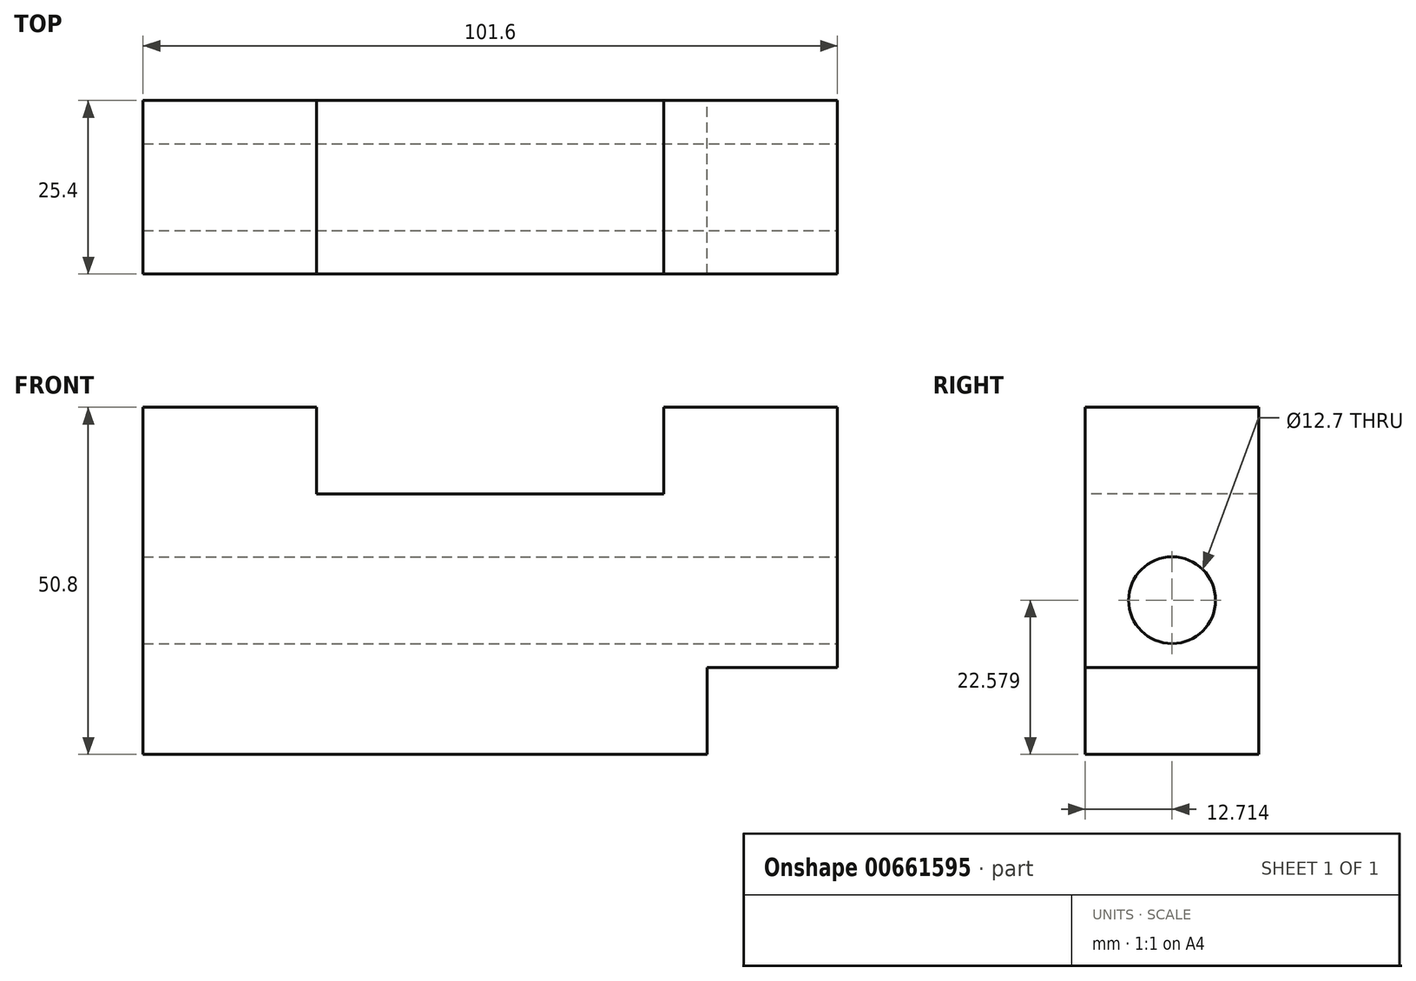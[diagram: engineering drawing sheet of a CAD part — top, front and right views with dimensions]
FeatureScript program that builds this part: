
annotation { "Feature Type Name" : "Feature", "Feature Type Description" : "" }
export const myFeature = defineFeature(function(context is Context, id is Id, definition is map)
    precondition{}
    {
        {
            var Q0;
            Q0=qCreatedBy(makeId("Front.planeOp"),FACE);
            var sketch = newSketch(context, id + "F0", { "sketchPlane" : qUnion([Q0])});
            skLineSegment(sketch, "E0.bottom", {"start": v(0, 0) * mm, "end": v(-101.6, 0) * mm});
            skLineSegment(sketch, "E0.top", {"start": v(0, 50.8) * mm, "end": v(-101.6, 50.8) * mm});
            skLineSegment(sketch, "E0.left", {"start": v(0, 0) * mm, "end": v(0, 50.8) * mm});
            skLineSegment(sketch, "E0.right", {"start": v(-101.6, 0) * mm, "end": v(-101.6, 50.8) * mm});
            skPoint(sketch, "E0.middle", {"position": v(-50.8, 25.4) * mm});
            skSolve(sketch);
        }
        {
            var Q0;
            Q0 = qSketchRegion(id + "F0", true);
            extrude(context, id + "F1", {"entities" : qUnion([Q0]), "depth" : 25.4 * mm, "offsetDistance" : 25.4 * mm});
        }
        {
            var Q0;
            Q0=makeQuery(id+"F1.opExtrude","CAP_FACE",FACE,{"disambiguationData":[OSD([sQuery(id+"F0.wireOp",EDGE,"E0.bottom"),sQuery(id+"F0.wireOp",EDGE,"E0.top"),sQuery(id+"F0.wireOp",EDGE,"E0.left"),sQuery(id+"F0.wireOp",EDGE,"E0.right")])],"isStart":false});
            var sketch = newSketch(context, id + "F2", { "sketchPlane" : qUnion([Q0])});
            skLineSegment(sketch, "E1.bottom", {"start": v(-25.4, 38.1) * mm, "end": v(-76.2, 38.1) * mm});
            skLineSegment(sketch, "E1.top", {"start": v(-25.4, 63.5) * mm, "end": v(-76.2, 63.5) * mm});
            skLineSegment(sketch, "E1.left", {"start": v(-25.4, 38.1) * mm, "end": v(-25.4, 63.5) * mm});
            skLineSegment(sketch, "E1.right", {"start": v(-76.2, 38.1) * mm, "end": v(-76.2, 63.5) * mm});
            skPoint(sketch, "E1.middle", {"position": v(-50.8, 50.8) * mm});
            skSolve(sketch);
        }
        {
            var Q0;
            {var subQ0=sQuery(id+"F2.wireOp",EDGE,"E1.bottom");Q0=makeQuery(id+"F2.imprint","IMPRINT",FACE,{"disambiguationData":[TD([[makeQuery(id+"F2.imprint","IMPRINT",EDGE,{"derivedFrom":subQ0}),-1.0]])]});}
            extrude(context, id + "F3", {"entities" : qUnion([Q0]), "operationType" : NewBodyOperationType.REMOVE, "endBound" : BoundingType.THROUGH_ALL, "oppositeDirection" : true, "depth" : 25.4 * mm, "offsetDistance" : 25.4 * mm});
        }
        {
            var Q0;
            Q0=makeQuery(id+"F1.opExtrude","SWEPT_FACE",FACE,{"disambiguationData":[OSD([sQuery(id+"F0.wireOp",EDGE,"E0.left")])]});
            var sketch = newSketch(context, id + "F4", { "sketchPlane" : qUnion([Q0])});
            skLineSegment(sketch, "E2.bottom", {"start": v(-25.4, 12.7) * mm, "end": v(0, 12.7) * mm});
            skLineSegment(sketch, "E2.top", {"start": v(-25.4, 0) * mm, "end": v(0, 0) * mm});
            skLineSegment(sketch, "E2.left", {"start": v(-25.4, 12.7) * mm, "end": v(-25.4, 0) * mm});
            skLineSegment(sketch, "E2.right", {"start": v(0, 12.7) * mm, "end": v(0, 0) * mm});
            skSolve(sketch);
        }
        {
            var Q0;
            Q0=makeQuery(id+"F4.imprint","IMPRINT",FACE,{"disambiguationData":[TD([[makeQuery(id+"F4.imprint","IMPRINT",EDGE,{"derivedFrom":sQuery(id+"F4.wireOp",EDGE,"E2.bottom")}),-1.0]])]});
            extrude(context, id + "F5", {"entities" : qUnion([Q0]), "operationType" : NewBodyOperationType.REMOVE, "oppositeDirection" : true, "depth" : 19.05 * mm, "offsetDistance" : 25.4 * mm});
        }
        {
            var Q0;
            Q0=makeQuery(id+"F1.opExtrude","SWEPT_FACE",FACE,{"disambiguationData":[OSD([sQuery(id+"F0.wireOp",EDGE,"E0.left")])]});
            var sketch = newSketch(context, id + "F6", { "sketchPlane" : qUnion([Q0])});
            skCircle(sketch, "E3", {"center": v(-12.69, 22.58) * mm, "radius": 6.35 * mm});
            skPoint(sketch, "E3.first.point", {"position": v(-17.65, 18.62) * mm});
            skPoint(sketch, "E3.second.point", {"position": v(-7.93, 26.78) * mm});
            skPoint(sketch, "E3.third.point", {"position": v(-12.18, 28.9) * mm});
            skSolve(sketch);
        }
        {
            var Q0;
            Q0=makeQuery(id+"F6.imprint","IMPRINT",FACE,{"disambiguationData":[TD([[makeQuery(id+"F6.imprint","IMPRINT",EDGE,{"derivedFrom":sQuery(id+"F6.wireOp",EDGE,"E3")}),1.0]])]});
            extrude(context, id + "F7", {"entities" : qUnion([Q0]), "operationType" : NewBodyOperationType.REMOVE, "endBound" : BoundingType.THROUGH_ALL, "oppositeDirection" : true, "depth" : 25.4 * mm, "offsetDistance" : 25.4 * mm});
        }
    });
